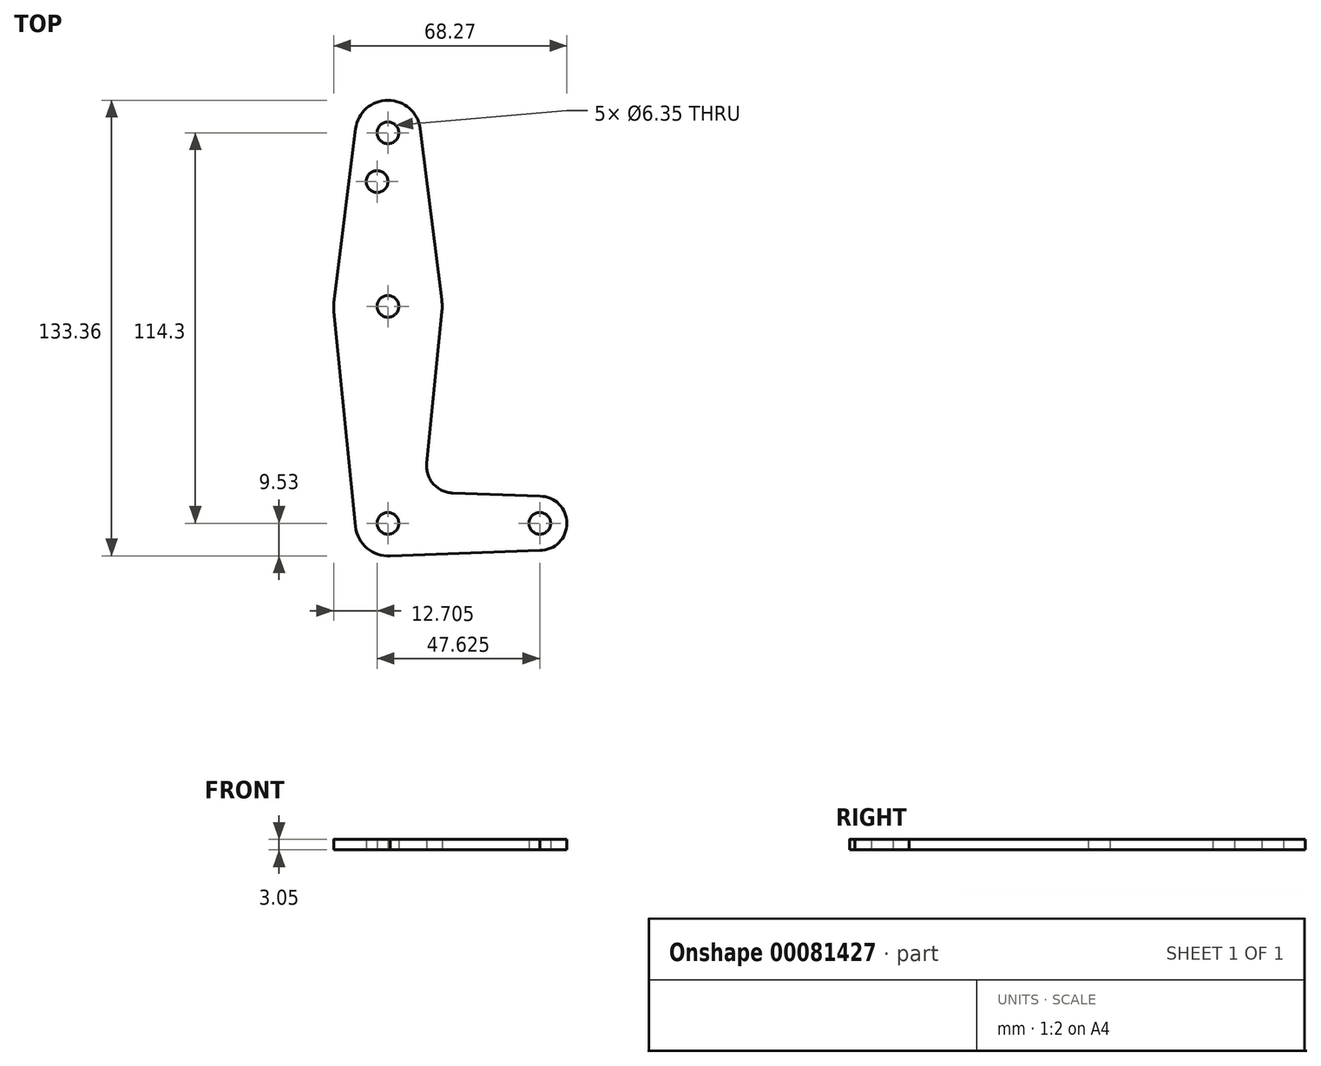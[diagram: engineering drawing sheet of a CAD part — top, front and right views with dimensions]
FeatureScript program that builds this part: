
annotation { "Feature Type Name" : "Feature", "Feature Type Description" : "" }
export const myFeature = defineFeature(function(context is Context, id is Id, definition is map)
    precondition{}
    {
        {
            var Q0;
            Q0=qCreatedBy(makeId("Top.planeOp"),FACE);
            var sketch = newSketch(context, id + "F0", { "sketchPlane" : qUnion([Q0])});
            skCircle(sketch, "E0", {"center": v(0, 0) * mm, "radius": 9.53 * mm});
            skCircle(sketch, "E1", {"center": v(0, 63.5) * mm, "radius": 15.88 * mm});
            skCircle(sketch, "E2", {"center": v(0, 114.3) * mm, "radius": 9.53 * mm});
            skCircle(sketch, "E3", {"center": v(44.45, 0) * mm, "radius": 7.94 * mm});
            skLineSegment(sketch, "E4", {"start": v(44.45, 0) * mm, "end": v(0, 0) * mm, "construction": true});
            skLineSegment(sketch, "E5", {"start": v(0, 114.3) * mm, "end": v(0, 63.5) * mm, "construction": true});
            skLineSegment(sketch, "E6", {"start": v(0, 0) * mm, "end": v(0, 63.5) * mm, "construction": true});
            skLineSegment(sketch, "E7", {"start": v(9.34, 116.39) * mm, "end": v(15.82, 64.9) * mm});
            skLineSegment(sketch, "E8", {"start": v(-9.34, 116.39) * mm, "end": v(-15.82, 64.9) * mm});
            skLineSegment(sketch, "E9", {"start": v(15.88, 62.78) * mm, "end": v(11.34, 17.59) * mm});
            skLineSegment(sketch, "E10", {"start": v(-15.88, 62.78) * mm, "end": v(-9.4, -1.76) * mm});
            skLineSegment(sketch, "E11", {"start": v(44.45, 7.94) * mm, "end": v(18.97, 8.85) * mm});
            skLineSegment(sketch, "E12", {"start": v(0, -9.53) * mm, "end": v(44.45, -7.94) * mm});
            skCircle(sketch, "E13", {"center": v(0, 114.3) * mm, "radius": 3.18 * mm});
            skCircle(sketch, "E14", {"center": v(0, 63.5) * mm, "radius": 3.18 * mm});
            skCircle(sketch, "E15", {"center": v(0, 0) * mm, "radius": 3.18 * mm});
            skCircle(sketch, "E16", {"center": v(44.45, 0) * mm, "radius": 3.18 * mm});
            skPoint(sketch, "E17.newPointB", {"position": v(9.4, -1.76) * mm});
            skArc(sketch, "E17.filletArc", {"start": v(11.34, 17.59) * mm, "mid": v(13.26, 11.57) * mm, "end": v(18.97, 8.85) * mm});
            skCircle(sketch, "E18", {"center": v(-3.17, 100.03) * mm, "radius": 3.18 * mm});
            skLineSegment(sketch, "E19", {"start": v(0, 100.03) * mm, "end": v(-3.18, 100.03) * mm, "construction": true});
            skSolve(sketch);
        }
        {
            var Q0;
            Q0 = qSketchRegion(id + "F0", true);
            extrude(context, id + "F1", {"entities" : qUnion([Q0]), "depth" : 3.05 * mm});
        }
    });
